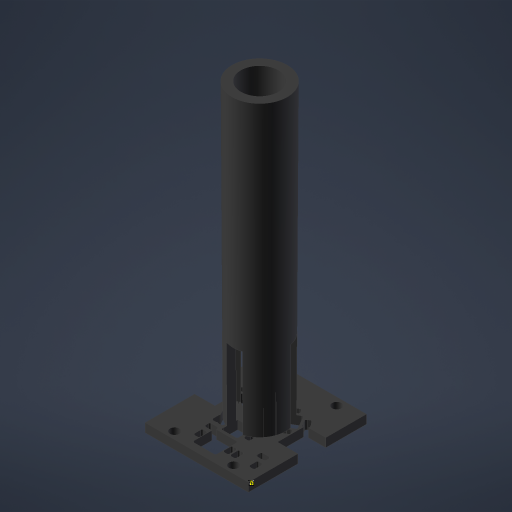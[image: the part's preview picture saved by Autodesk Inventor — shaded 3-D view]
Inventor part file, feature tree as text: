
AUTODESK INVENTOR PART (.ipt)
format: ipt  version: 2024.1 (Build 281209000, 209)  size: 1,758,720 bytes
history: native  units: mm
features: projected_geometry x23, sketch x18, extrude x14, plane x2, loft x2
ambient origin geometry x8: Origin, YZ Plane, XZ Plane, XY Plane, X Axis, Y Axis, Z Axis, Center Point
bodies: Solid1 (feature_tree), Solid2 (feature_tree)
feature tree (59):
  extrude  "Extrusion1"  Depth=3.0mm
  extrude  "Extrusion2"  TaperAngle=0.0deg  [1 undecoded]
  extrude  "Extrusion3"  Depth=10.0mm TaperAngle=0.0deg
  extrude  "Extrusion4"  Depth=0.5mm
  extrude  "Extrusion5"  Depth=0.5mm
  sketch  "Sketch6"  dims[d14=0.5mm d15=0.5mm]
  plane  "Work Plane1"
  loft  "Loft1"
  loft  "Loft2"
  extrude  "Extrusion6"  Depth=0.5mm
  extrude  "Extrusion8"  Depth=0.5mm
  extrude  "Extrusion9"  Depth=0.5mm
  extrude  "Extrusion10"  Depth=0.5mm
  extrude  "Extrusion11"  Depth=0.5mm
  extrude  "Extrusion12"  Depth=0.5mm
  plane  "Work Plane2"
  sketch  "Sketch19"  dims[d34=0.5mm d35=0.5mm]
  extrude  "Extrusion13"  Depth=0.5mm
  extrude  "Extrusion14"  Depth=0.5mm
  extrude  "Extrusion15"  Depth=0.5mm
  sketch  "Sketch1"  dims[d0=3.0mm d1=0.0mm d2=0.2mm]
  sketch  "Sketch2"  dims[d3=1.0mm d4=0.0mm d5=0.0mm]
  sketch  "Sketch3"  dims[d6=10.0mm d7=0.0mm d8=10.0mm d9=0.0mm]
  sketch  "Sketch4"  dims[d10=0.5mm d11=0.5mm]
  sketch  "Sketch5"  dims[d12=0.5mm d13=0.5mm]
  sketch  "Sketch7"  dims[d16=0.5mm d17=0.5mm]
  sketch  "Sketch8"  dims[d18=0.5mm d19=0.5mm]
  sketch  "Sketch9"  dims[d20=0.5mm d21=0.5mm]
  sketch  "Sketch11"  dims[d22=0.5mm d23=0.5mm]
  sketch  "Sketch13"  dims[d24=0.5mm d25=0.5mm]
  projected_geometry  "Projected Loop2"
  projected_geometry  "Projected Loop3"
  projected_geometry  "Projected Loop4"
  projected_geometry  "Projected Loop5"
  projected_geometry  "Projected Loop6"
  projected_geometry  "Projected Loop7"
  projected_geometry  "Projected Loop8"
  projected_geometry  "Projected Loop9"
  projected_geometry  "Projected Loop10"
  projected_geometry  "Projected Loop11"
  projected_geometry  "Projected Loop12"
  projected_geometry  "Projected Loop13"
  projected_geometry  "Projected Loop14"
  projected_geometry  "Projected Loop15"
  projected_geometry  "Projected Loop16"
  projected_geometry  "Projected Loop17"
  sketch  "Sketch14"  dims[d26=0.5mm d27=0.5mm]
  sketch  "Sketch15"  dims[d28=0.5mm d29=0.5mm]
  projected_geometry  "Projected Loop18"
  sketch  "Sketch16"  dims[d30=0.5mm d31=0.5mm]
  sketch  "Sketch17"  dims[d32=0.5mm d33=0.5mm]
  projected_geometry  "Projected Loop19"
  sketch  "Sketch20"  dims[d36=0.5mm]
  sketch  "Sketch21"  dims[d37=0.5mm d38=10.0mm d39=0.0mm d40=12.0mm d41=100.0mm d42=13.0mm d43=3.0mm d44=3.0mm d45=0.0mm d46=90.0deg d47=0.0mm d48=90.0deg d49=13.0mm d50=0.0mm d51=90.0deg d52=0.0mm d53=90.0deg d55=7.0mm d56=17.0mm d57=14.0mm d58=0.0mm d59=0.0mm d64=25.0mm d65=0.0mm d66=25.0mm d67=0.0mm d68=25.0mm d69=0.0mm d70=3.0mm d71=1.0mm d72=1.0mm d73=10.0mm d74=0.0mm d75=10.0mm d76=0.0mm d78=2.0mm d79=0.0mm d80=0.3mm d81=0.0mm d82=0.3mm d83=0.0mm]
  projected_geometry  "Projected Loop20"
  projected_geometry  "Project Cut Edges1"
  projected_geometry  "Project Cut Edges2"
  projected_geometry  "Project Cut Edges3"
  projected_geometry  "Project Cut Edges5"
note: 1 required parameter value undecoded (feature->parameter linkage not recoverable at this tier; creation-order binding heuristic only, values carry confidence <= 0.55)
